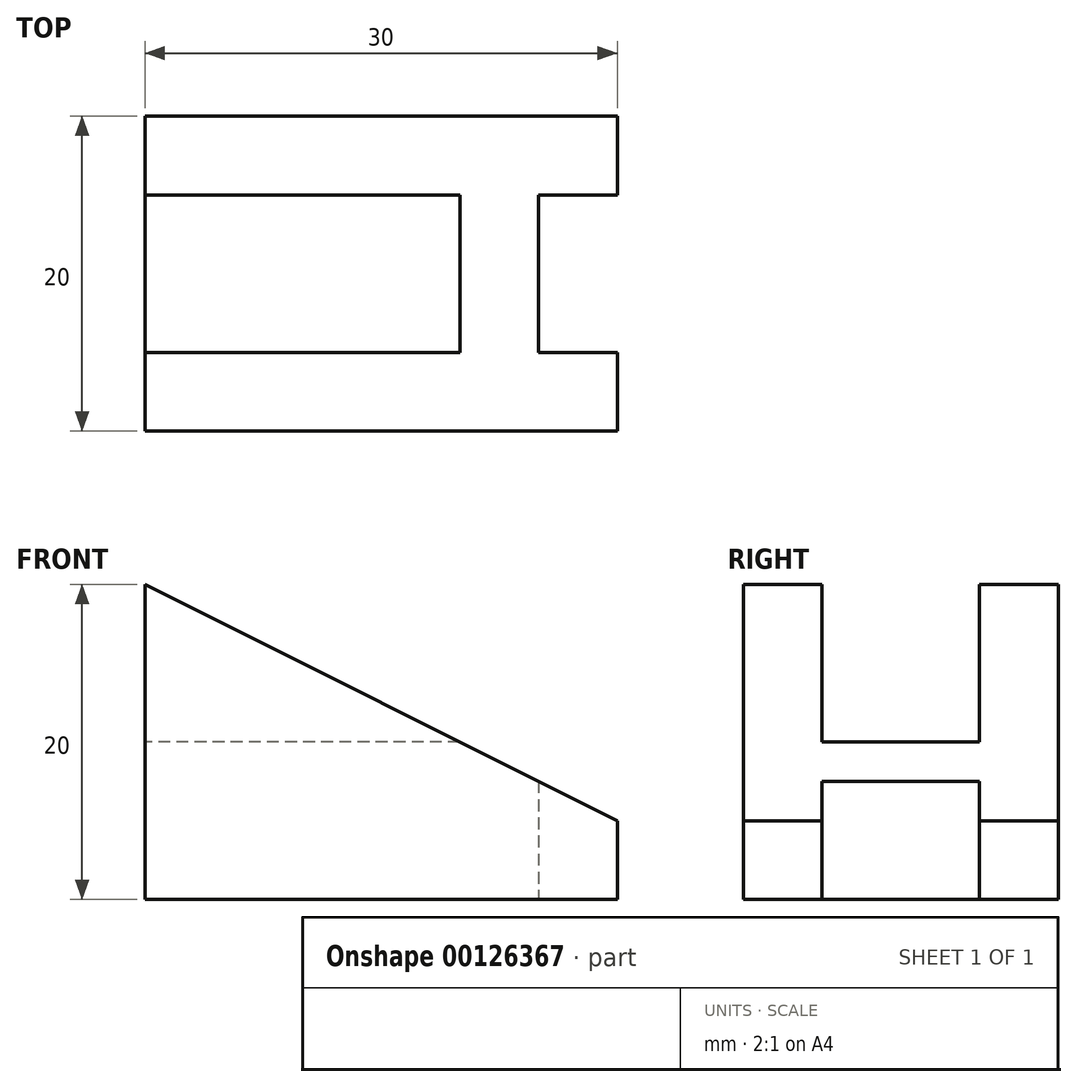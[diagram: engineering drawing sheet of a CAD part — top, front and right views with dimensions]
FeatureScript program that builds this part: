
annotation { "Feature Type Name" : "Feature", "Feature Type Description" : "" }
export const myFeature = defineFeature(function(context is Context, id is Id, definition is map)
    precondition{}
    {
        {
            var Q0;
            Q0=qCreatedBy(makeId("Front.planeOp"),FACE);
            var sketch = newSketch(context, id + "F0", { "sketchPlane" : qUnion([Q0])});
            skLineSegment(sketch, "E0", {"start": v(0, 0) * mm, "end": v(0, 20) * mm});
            skLineSegment(sketch, "E1", {"start": v(0, 0) * mm, "end": v(30, 0) * mm});
            skLineSegment(sketch, "E2", {"start": v(30, 0) * mm, "end": v(30, 5) * mm});
            skLineSegment(sketch, "E3", {"start": v(30, 5) * mm, "end": v(0, 20) * mm});
            skSolve(sketch);
        }
        {
            var Q0;
            Q0 = qSketchRegion(id + "F0", true);
            extrude(context, id + "F1", {"entities" : qUnion([Q0]), "oppositeDirection" : true, "depth" : 20 * mm});
        }
        {
            var Q0;
            Q0=makeQuery(id+"F1.opExtrude","SWEPT_FACE",FACE,{"disambiguationData":[OSD([sQuery(id+"F0.wireOp",EDGE,"E0")])]});
            var sketch = newSketch(context, id + "F2", { "sketchPlane" : qUnion([Q0])});
            skLineSegment(sketch, "E4.bottom", {"start": v(-15, 20) * mm, "end": v(-5, 20) * mm});
            skLineSegment(sketch, "E4.top", {"start": v(-15, 10) * mm, "end": v(-5, 10) * mm});
            skLineSegment(sketch, "E4.left", {"start": v(-15, 20) * mm, "end": v(-15, 10) * mm});
            skLineSegment(sketch, "E4.right", {"start": v(-5, 20) * mm, "end": v(-5, 10) * mm});
            skSolve(sketch);
        }
        {
            var Q0;
            Q0 = qSketchRegion(id + "F2", true);
            extrude(context, id + "F3", {"entities" : qUnion([Q0]), "operationType" : NewBodyOperationType.REMOVE, "endBound" : BoundingType.THROUGH_ALL, "oppositeDirection" : true, "depth" : 25 * mm});
        }
        {
            var Q0;
            Q0=makeQuery(id+"F1.opExtrude","SWEPT_FACE",FACE,{"disambiguationData":[OSD([sQuery(id+"F0.wireOp",EDGE,"E1")])]});
            var sketch = newSketch(context, id + "F4", { "sketchPlane" : qUnion([Q0])});
            skLineSegment(sketch, "E5.bottom", {"start": v(30, -5) * mm, "end": v(25, -5) * mm});
            skLineSegment(sketch, "E5.top", {"start": v(30, -15) * mm, "end": v(25, -15) * mm});
            skLineSegment(sketch, "E5.left", {"start": v(30, -5) * mm, "end": v(30, -15) * mm});
            skLineSegment(sketch, "E5.right", {"start": v(25, -5) * mm, "end": v(25, -15) * mm});
            skSolve(sketch);
        }
        {
            var Q0;
            Q0 = qSketchRegion(id + "F4", true);
            extrude(context, id + "F5", {"entities" : qUnion([Q0]), "operationType" : NewBodyOperationType.REMOVE, "endBound" : BoundingType.THROUGH_ALL, "oppositeDirection" : true, "depth" : 25 * mm});
        }
    });
